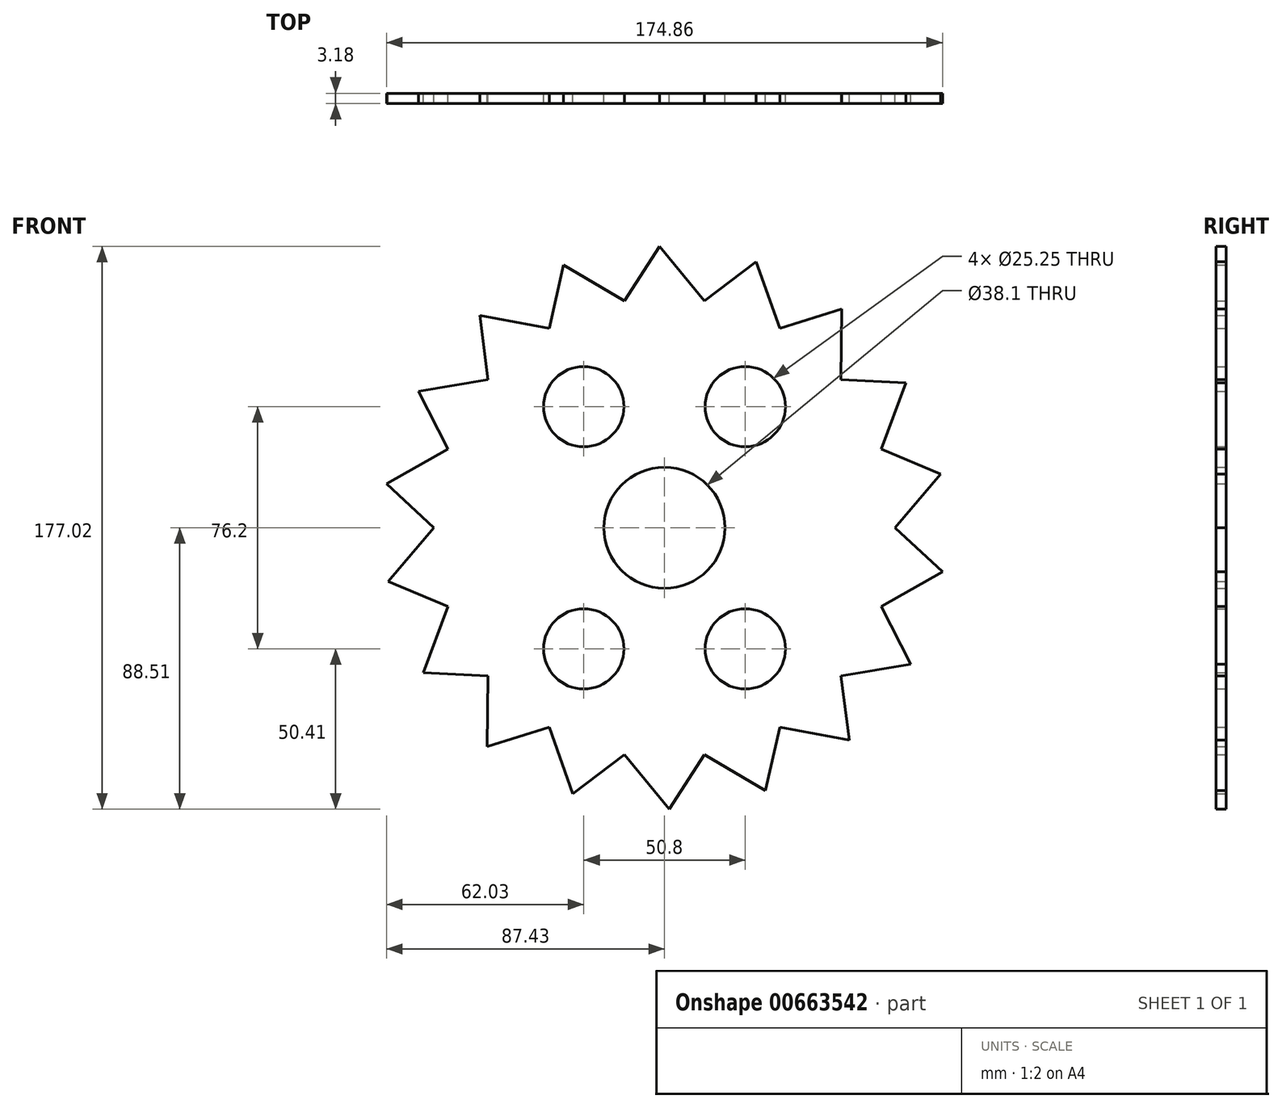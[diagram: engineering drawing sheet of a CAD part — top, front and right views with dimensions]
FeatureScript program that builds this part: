
annotation { "Feature Type Name" : "Feature", "Feature Type Description" : "" }
export const myFeature = defineFeature(function(context is Context, id is Id, definition is map)
    precondition{}
    {
        {
            var Q0;
            Q0=qCreatedBy(makeId("Front.planeOp"),FACE);
            var sketch = newSketch(context, id + "F0", { "sketchPlane" : qUnion([Q0])});
            skCircle(sketch, "E0", {"center": v(0, 0) * mm, "radius": 72.49 * mm});
            skCircle(sketch, "E1", {"center": v(0, 0) * mm, "radius": 88.52 * mm, "construction": true});
            skLineSegment(sketch, "E2", {"start": v(0, 0) * mm, "end": v(-102.12, 0) * mm, "construction": true});
            skLineSegment(sketch, "E3", {"start": v(0, 0) * mm, "end": v(-98.32, 35.79) * mm, "construction": true});
            skLineSegment(sketch, "E4", {"start": v(-72.49, 0) * mm, "end": v(-87.43, 13.85) * mm});
            skLineSegment(sketch, "E5", {"start": v(-87.43, 13.85) * mm, "end": v(-68.11, 24.8) * mm});
            skLineSegment(sketch, "E6.1.0", {"start": v(-68.11, 24.8) * mm, "end": v(-77.43, 42.92) * mm});
            skLineSegment(sketch, "E6.1.1", {"start": v(-77.43, 42.92) * mm, "end": v(-55.53, 46.6) * mm});
            skLineSegment(sketch, "E6.2.0", {"start": v(-55.53, 46.6) * mm, "end": v(-58.08, 66.8) * mm});
            skLineSegment(sketch, "E6.2.1", {"start": v(-58.08, 66.8) * mm, "end": v(-36.24, 62.77) * mm});
            skLineSegment(sketch, "E6.3.0", {"start": v(-36.24, 62.77) * mm, "end": v(-31.73, 82.64) * mm});
            skLineSegment(sketch, "E6.3.1", {"start": v(-31.73, 82.64) * mm, "end": v(-12.59, 71.38) * mm});
            skLineSegment(sketch, "E6.4.0", {"start": v(-12.59, 71.38) * mm, "end": v(-1.55, 88.51) * mm});
            skLineSegment(sketch, "E6.4.1", {"start": v(-1.55, 88.51) * mm, "end": v(12.59, 71.38) * mm});
            skLineSegment(sketch, "E6.5.0", {"start": v(12.59, 71.38) * mm, "end": v(28.82, 83.7) * mm});
            skLineSegment(sketch, "E6.5.1", {"start": v(28.82, 83.7) * mm, "end": v(36.24, 62.77) * mm});
            skLineSegment(sketch, "E6.6.0", {"start": v(36.24, 62.77) * mm, "end": v(55.7, 68.8) * mm});
            skLineSegment(sketch, "E6.6.1", {"start": v(55.7, 68.8) * mm, "end": v(55.53, 46.6) * mm});
            skLineSegment(sketch, "E6.7.0", {"start": v(55.53, 46.6) * mm, "end": v(75.88, 45.6) * mm});
            skLineSegment(sketch, "E6.7.1", {"start": v(75.88, 45.6) * mm, "end": v(68.11, 24.8) * mm});
            skLineSegment(sketch, "E6.8.0", {"start": v(68.11, 24.8) * mm, "end": v(86.9, 16.9) * mm});
            skLineSegment(sketch, "E6.8.1", {"start": v(86.9, 16.9) * mm, "end": v(72.49, 0) * mm});
            skLineSegment(sketch, "E6.9.0", {"start": v(72.49, 0) * mm, "end": v(87.43, -13.85) * mm});
            skLineSegment(sketch, "E6.9.1", {"start": v(87.43, -13.85) * mm, "end": v(68.11, -24.8) * mm});
            skLineSegment(sketch, "E6.10.0", {"start": v(68.11, -24.8) * mm, "end": v(77.43, -42.92) * mm});
            skLineSegment(sketch, "E6.10.1", {"start": v(77.43, -42.92) * mm, "end": v(55.53, -46.6) * mm});
            skLineSegment(sketch, "E6.11.0", {"start": v(55.53, -46.6) * mm, "end": v(58.08, -66.8) * mm});
            skLineSegment(sketch, "E6.11.1", {"start": v(58.08, -66.8) * mm, "end": v(36.24, -62.77) * mm});
            skLineSegment(sketch, "E6.12.0", {"start": v(36.24, -62.77) * mm, "end": v(31.73, -82.64) * mm});
            skLineSegment(sketch, "E6.12.1", {"start": v(31.73, -82.64) * mm, "end": v(12.59, -71.38) * mm});
            skLineSegment(sketch, "E6.13.0", {"start": v(12.59, -71.38) * mm, "end": v(1.55, -88.51) * mm});
            skLineSegment(sketch, "E6.13.1", {"start": v(1.55, -88.51) * mm, "end": v(-12.59, -71.38) * mm});
            skLineSegment(sketch, "E6.14.0", {"start": v(-12.59, -71.38) * mm, "end": v(-28.82, -83.7) * mm});
            skLineSegment(sketch, "E6.14.1", {"start": v(-28.82, -83.7) * mm, "end": v(-36.24, -62.77) * mm});
            skLineSegment(sketch, "E6.15.0", {"start": v(-36.24, -62.77) * mm, "end": v(-55.7, -68.8) * mm});
            skLineSegment(sketch, "E6.15.1", {"start": v(-55.7, -68.8) * mm, "end": v(-55.53, -46.6) * mm});
            skLineSegment(sketch, "E6.16.0", {"start": v(-55.53, -46.6) * mm, "end": v(-75.88, -45.6) * mm});
            skLineSegment(sketch, "E6.16.1", {"start": v(-75.88, -45.6) * mm, "end": v(-68.11, -24.8) * mm});
            skLineSegment(sketch, "E6.17.0", {"start": v(-68.11, -24.8) * mm, "end": v(-86.9, -16.9) * mm});
            skLineSegment(sketch, "E6.17.1", {"start": v(-86.9, -16.9) * mm, "end": v(-72.49, 0) * mm});
            skLineSegment(sketch, "E6.anchor1", {"start": v(0, 0) * mm, "end": v(-87.43, 13.85) * mm, "construction": true});
            skLineSegment(sketch, "E6.anchor2", {"start": v(0, 0) * mm, "end": v(-86.9, -16.9) * mm, "construction": true});
            skCircle(sketch, "E7", {"center": v(25.4, 38.1) * mm, "radius": 12.62 * mm});
            skCircle(sketch, "E8.MirrorC", {"center": v(25.4, -38.1) * mm, "radius": 12.62 * mm});
            skCircle(sketch, "E9.MirrorC", {"center": v(-25.4, 38.1) * mm, "radius": 12.62 * mm});
            skCircle(sketch, "E10.MirrorC", {"center": v(-25.4, -38.1) * mm, "radius": 12.62 * mm});
            skCircle(sketch, "E11", {"center": v(0, 0) * mm, "radius": 19.05 * mm});
            skSolve(sketch);
        }
        {
            var Q0;
            Q0 = qSketchRegion(id + "F0", true);
            extrude(context, id + "F1", {"entities" : qUnion([Q0]), "depth" : 3.17 * mm, "offsetDistance" : 25.4 * mm});
        }
    });
